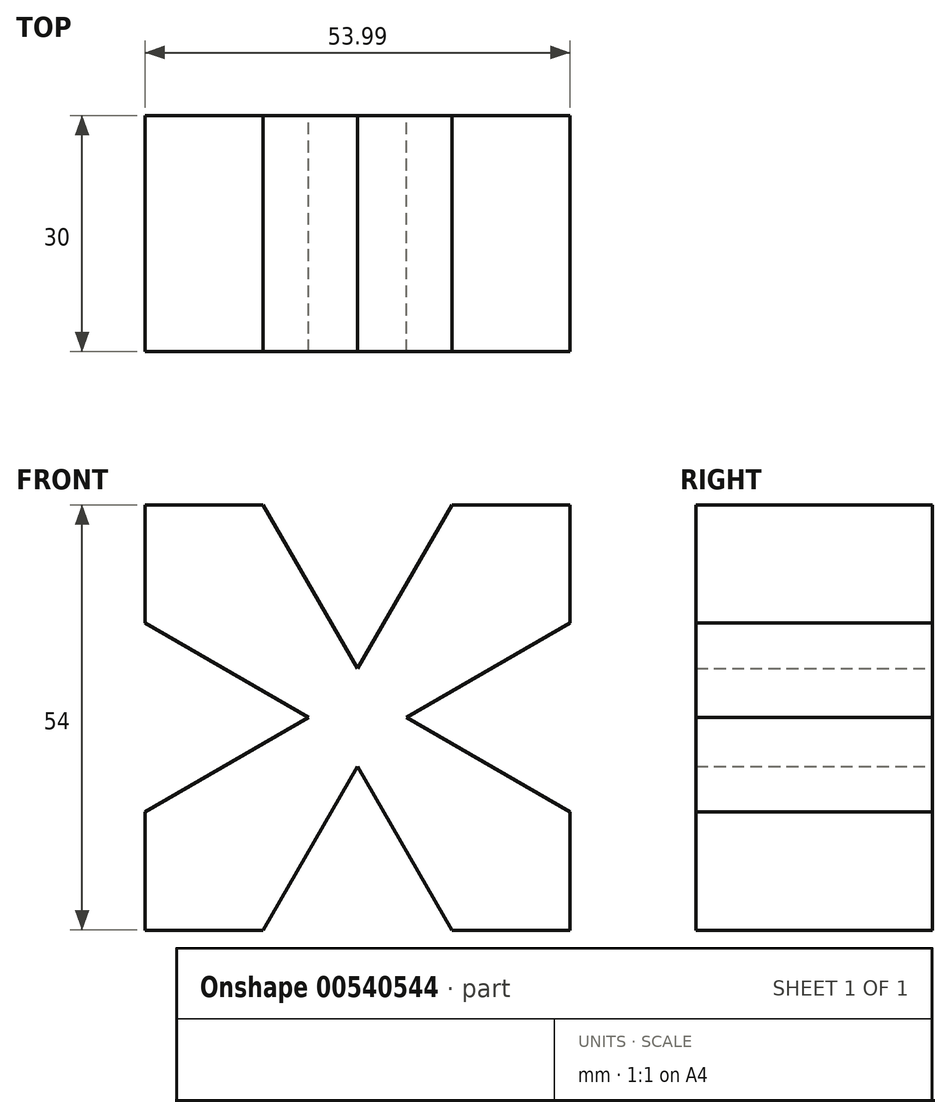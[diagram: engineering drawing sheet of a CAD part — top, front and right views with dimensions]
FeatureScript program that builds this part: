
annotation { "Feature Type Name" : "Feature", "Feature Type Description" : "" }
export const myFeature = defineFeature(function(context is Context, id is Id, definition is map)
    precondition{}
    {
        {
            var Q0;
            Q0=qCreatedBy(makeId("Front.planeOp"),FACE);
            var sketch = newSketch(context, id + "F0", { "sketchPlane" : qUnion([Q0])});
            skLineSegment(sketch, "E0.bottom", {"start": v(-27.97, 25.47) * mm, "end": v(-12.97, 25.47) * mm});
            skLineSegment(sketch, "E0.top", {"start": v(-27.97, -28.53) * mm, "end": v(-12.97, -28.53) * mm});
            skLineSegment(sketch, "E0.left", {"start": v(-27.97, 25.47) * mm, "end": v(-27.97, 10.47) * mm});
            skLineSegment(sketch, "E0.right", {"start": v(26.02, -13.53) * mm, "end": v(26.02, -28.53) * mm});
            skPoint(sketch, "E1", {"position": v(-12.97, -28.53) * mm});
            skPoint(sketch, "E2", {"position": v(11.02, -28.53) * mm});
            skPoint(sketch, "E3", {"position": v(26.02, -13.53) * mm});
            skPoint(sketch, "E4", {"position": v(26.02, 10.47) * mm});
            skPoint(sketch, "E5", {"position": v(11.02, 25.47) * mm});
            skPoint(sketch, "E6", {"position": v(-12.97, 25.47) * mm});
            skPoint(sketch, "E7", {"position": v(-27.97, 10.47) * mm});
            skPoint(sketch, "E8", {"position": v(-27.97, -13.53) * mm});
            skLineSegment(sketch, "E9", {"start": v(-12.97, -28.53) * mm, "end": v(-0.97, -7.75) * mm});
            skLineSegment(sketch, "E10", {"start": v(-0.97, -7.75) * mm, "end": v(11.02, -28.53) * mm});
            skLineSegment(sketch, "E11", {"start": v(26.02, -13.53) * mm, "end": v(5.24, -1.53) * mm});
            skLineSegment(sketch, "E12", {"start": v(-27.97, -13.53) * mm, "end": v(-7.18, -1.53) * mm});
            skLineSegment(sketch, "E13", {"start": v(-27.97, 10.47) * mm, "end": v(-7.18, -1.53) * mm});
            skLineSegment(sketch, "E14", {"start": v(26.02, 10.47) * mm, "end": v(5.24, -1.53) * mm});
            skLineSegment(sketch, "E15", {"start": v(-12.97, 25.47) * mm, "end": v(-0.97, 4.68) * mm});
            skLineSegment(sketch, "E16", {"start": v(11.02, 25.47) * mm, "end": v(-0.97, 4.68) * mm});
            skLineSegment(sketch, "E17.trimOffspring", {"start": v(11.02, 25.47) * mm, "end": v(26.02, 25.47) * mm});
            skLineSegment(sketch, "E18.trimOffspring", {"start": v(11.02, -28.53) * mm, "end": v(26.02, -28.53) * mm});
            skLineSegment(sketch, "E19.trimOffspring", {"start": v(-27.97, -13.53) * mm, "end": v(-27.97, -28.53) * mm});
            skLineSegment(sketch, "E20", {"start": v(26.02, 25.47) * mm, "end": v(26.02, 10.47) * mm});
            skSolve(sketch);
        }
        {
            var Q0;
            Q0 = qSketchRegion(id + "F0", true);
            extrude(context, id + "F1", {"entities" : qUnion([Q0]), "depth" : 30 * mm, "offsetDistance" : 25 * mm});
        }
    });
